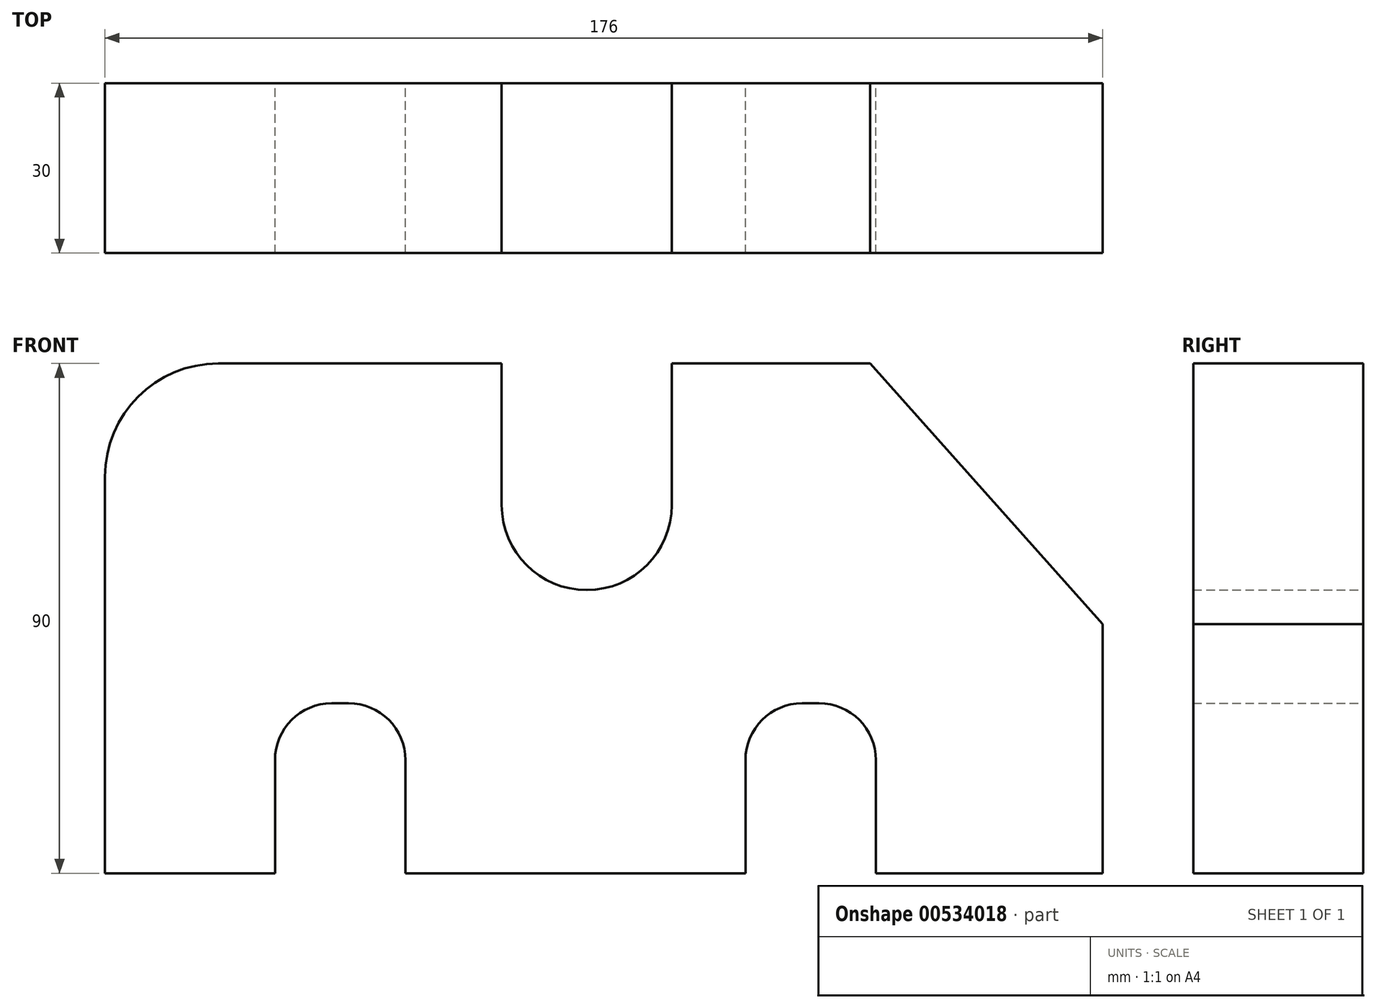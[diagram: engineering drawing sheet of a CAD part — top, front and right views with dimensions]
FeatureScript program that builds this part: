
annotation { "Feature Type Name" : "Feature", "Feature Type Description" : "" }
export const myFeature = defineFeature(function(context is Context, id is Id, definition is map)
    precondition{}
    {
        {
            var Q0;
            Q0=qCreatedBy(makeId("Front.planeOp"),FACE);
            var sketch = newSketch(context, id + "F0", { "sketchPlane" : qUnion([Q0])});
            skLineSegment(sketch, "E0", {"start": v(-103.5, -45.05) * mm, "end": v(-73.5, -45.05) * mm});
            skLineSegment(sketch, "E1", {"start": v(-73.5, -45.05) * mm, "end": v(-73.5, -25.05) * mm});
            skLineSegment(sketch, "E2", {"start": v(-63.5, -15.05) * mm, "end": v(-60.5, -15.05) * mm});
            skLineSegment(sketch, "E3", {"start": v(-50.5, -25.05) * mm, "end": v(-50.5, -45.05) * mm});
            skLineSegment(sketch, "E4", {"start": v(-50.5, -45.05) * mm, "end": v(9.5, -45.05) * mm});
            skLineSegment(sketch, "E5", {"start": v(9.5, -45.05) * mm, "end": v(9.5, -25.05) * mm});
            skLineSegment(sketch, "E6", {"start": v(19.5, -15.05) * mm, "end": v(22.5, -15.05) * mm});
            skLineSegment(sketch, "E7", {"start": v(32.5, -25.05) * mm, "end": v(32.5, -45.05) * mm});
            skLineSegment(sketch, "E8", {"start": v(32.5, -45.05) * mm, "end": v(72.5, -45.05) * mm});
            skLineSegment(sketch, "E9", {"start": v(72.5, -45.05) * mm, "end": v(72.5, -1.05) * mm});
            skPoint(sketch, "E10.visualSharp", {"position": v(-73.5, -15.05) * mm});
            skArc(sketch, "E10.filletArc", {"start": v(-63.5, -15.05) * mm, "mid": v(-70.57, -17.98) * mm, "end": v(-73.5, -25.05) * mm});
            skPoint(sketch, "E11.visualSharp", {"position": v(9.5, -15.05) * mm});
            skArc(sketch, "E11.filletArc", {"start": v(19.5, -15.05) * mm, "mid": v(12.43, -17.98) * mm, "end": v(9.5, -25.05) * mm});
            skPoint(sketch, "E12.visualSharp", {"position": v(32.5, -15.05) * mm});
            skArc(sketch, "E12.filletArc", {"start": v(32.5, -25.05) * mm, "mid": v(29.57, -17.98) * mm, "end": v(22.5, -15.05) * mm});
            skPoint(sketch, "E13.visualSharp", {"position": v(-50.5, -15.05) * mm});
            skArc(sketch, "E13.filletArc", {"start": v(-50.5, -25.05) * mm, "mid": v(-53.43, -17.98) * mm, "end": v(-60.5, -15.05) * mm});
            skLineSegment(sketch, "E14", {"start": v(-103.5, -45.05) * mm, "end": v(-103.5, 24.95) * mm});
            skLineSegment(sketch, "E15", {"start": v(-83.5, 44.95) * mm, "end": v(-33.5, 44.95) * mm});
            skPoint(sketch, "E16.visualSharp", {"position": v(-103.5, 44.95) * mm});
            skArc(sketch, "E16.filletArc", {"start": v(-83.5, 44.95) * mm, "mid": v(-97.64, 39.09) * mm, "end": v(-103.5, 24.95) * mm});
            skLineSegment(sketch, "E17", {"start": v(-33.5, 44.95) * mm, "end": v(-33.5, 19.95) * mm});
            skLineSegment(sketch, "E18", {"start": v(-18.5, 4.95) * mm, "end": v(-18.5, 4.95) * mm});
            skLineSegment(sketch, "E19", {"start": v(-3.5, 19.95) * mm, "end": v(-3.5, 44.95) * mm});
            skLineSegment(sketch, "E20", {"start": v(-3.5, 44.95) * mm, "end": v(31.5, 44.95) * mm});
            skLineSegment(sketch, "E21", {"start": v(31.5, 44.95) * mm, "end": v(72.5, -1.05) * mm});
            skPoint(sketch, "E22.visualSharp", {"position": v(-33.5, 4.95) * mm});
            skArc(sketch, "E22.filletArc", {"start": v(-33.5, 19.95) * mm, "mid": v(-29.1, 9.34) * mm, "end": v(-18.5, 4.95) * mm});
            skPoint(sketch, "E23.visualSharp", {"position": v(-3.5, 4.95) * mm});
            skArc(sketch, "E23.filletArc", {"start": v(-18.5, 4.95) * mm, "mid": v(-7.9, 9.34) * mm, "end": v(-3.5, 19.95) * mm});
            skSolve(sketch);
        }
        {
            var Q0;
            Q0 = qSketchRegion(id + "F0", true);
            extrude(context, id + "F1", {"entities" : qUnion([Q0]), "depth" : 30 * mm, "offsetDistance" : 25 * mm});
        }
    });
